# Revit family: NBS_DudleyIndustriesLimited_PprTwlDpnsrs_PlatinumRollerTowelCabinet
name_source: partatom
category: Furniture
revit_build: Autodesk Revit 2018 (Build: 20190510_1515(x64)
units: mm (PartAtom-declared; Revit-internal decimal feet)

## family parameters
Cut with Voids When Loaded = No
Host = Face
Room Calculation Point = No
Shared = No

## types (1)
- PlatinumRollerTowelCabinet
    AssetType = Fixed
    BIMObjectName = NBS_DudleyIndustriesLimited_TowelRails_PlatinumRollerTowelCabinet
    CabinetMaterial = NBS_DudleyIndustriesLimited_StainlessSteel_Brushed
    Category = Pr_40_70_22_62:Paper towel dispensers
    Default Elevation = 1300 mm  [stored 4.26509 ft]
    Description = Clearview roller towel cabinet
    DurationUnit = year
    Features = Automatically locks on closure, innovative coating helps prevent fingerprint marks, east to wipe clean
    Finish = Brushed with clear lacquer
    FinishAndColour = Brushed with clear lacquer
    IfcExportAs = IfcFurnitureType
    IfcExportType = UNDEFINED
    IsBuiltIn = Yes
    ManufacturerName = Dudley Industries Limited
    ManufacturerURL = www.dudleyindustries.com
    Material = Cabinet: Stainless steel, Reservoir: Plastic
    Materials = Cabinet: Stainless steel, Reservoir: Plastic
    ModelNumber = 41600CB
    ModelReference = PlatinumRollerTowelCabinet
    NBSCertification = www.nationalbimlibrary.com/cert/tsef3lt1
    NBSDescription = Paper towel dispensers
    NBSReference = 45-35-72/344
    Name = PaperTowelDispensers_PlatinumRollerTowelCabinet_DudleyIndustriesLimited
    NominalDepth = 275 mm
    NominalHeight = 480 mm  [stored 1.5748 ft]
    NominalLength = 0 mm  [stored 0 ft]
    NominalWidth = 405 mm
    ProductInformation = https://www.dudleyindustries.com
    ReservoirMaterial = NBS_DudleyIndustriesLimited_ABSPlastic_ClearTinted
    Shape = Rectangular
    Size = 275 x 480 x 405 mm
    Status = UNSET
    Style = Cabinet
    Uniclass2015Code = Pr_40_70_22_62
    Uniclass2015Title = Paper towel dispensers
    Uniclass2015Version = Products v1.18
    Version = 1
    WarrantyDurationUnit = year
    Weight = 7.14 kg

note: [stored X ft] marks values corroborated as IEEE doubles in the binary element streams (Revit-internal decimal feet)

## geometry (parser evidence)
native form markers: Sweep x2
no freeform markers — native parametric forms only
